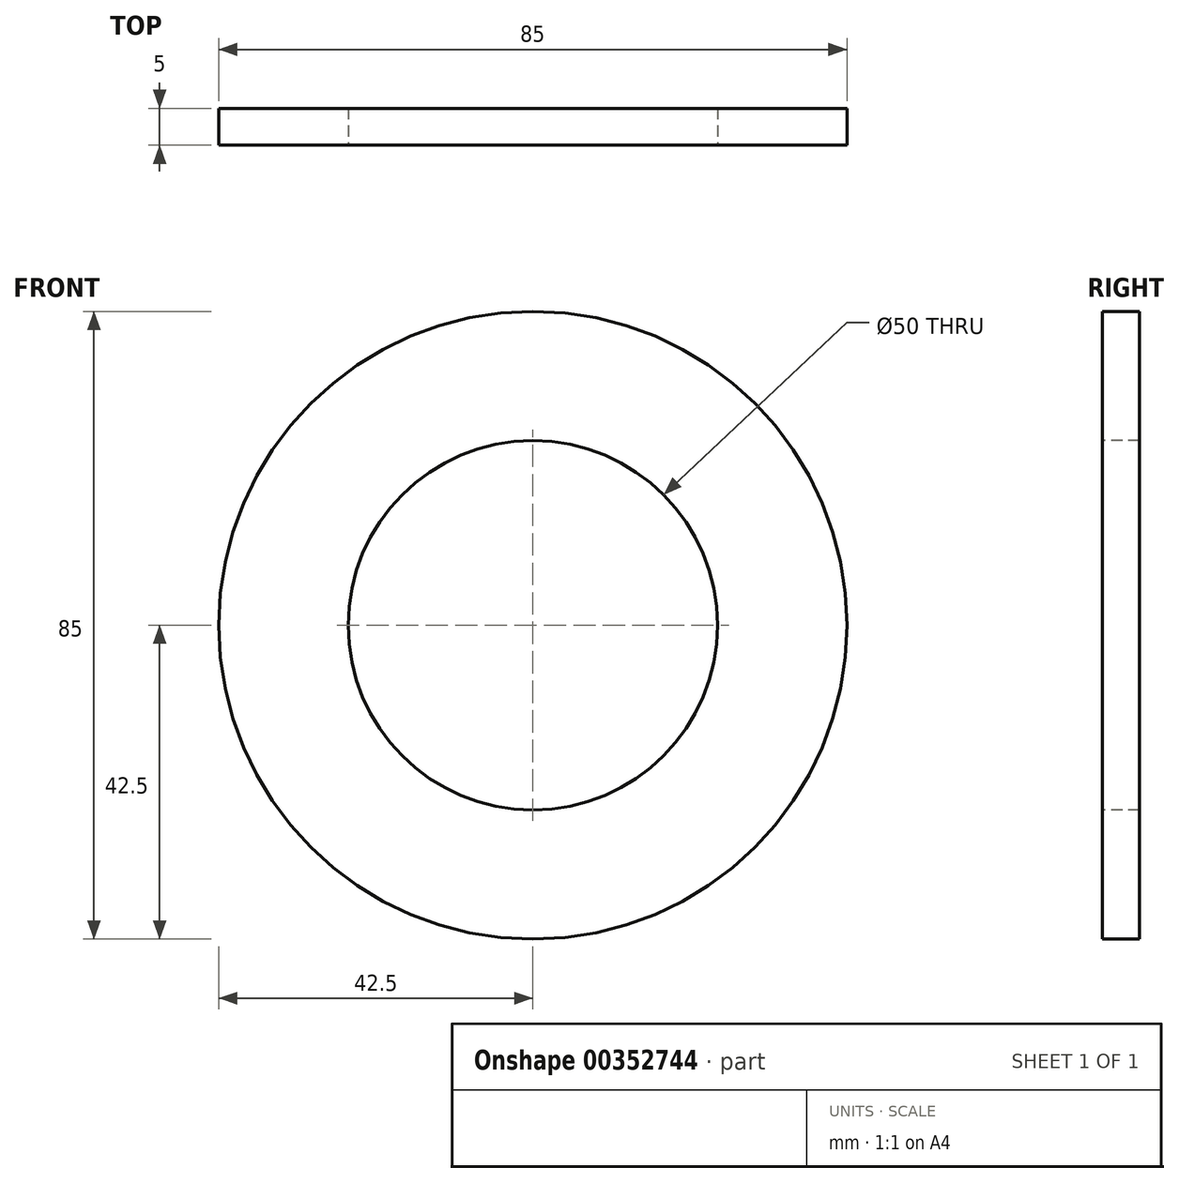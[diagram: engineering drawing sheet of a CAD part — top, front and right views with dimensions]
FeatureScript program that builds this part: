
annotation { "Feature Type Name" : "Feature", "Feature Type Description" : "" }
export const myFeature = defineFeature(function(context is Context, id is Id, definition is map)
    precondition{}
    {
        {
            var Q0;
            Q0=qCreatedBy(makeId("Front.planeOp"),FACE);
            var sketch = newSketch(context, id + "F0", { "sketchPlane" : qUnion([Q0])});
            skCircle(sketch, "E0", {"center": v(0, 0) * mm, "radius": 25 * mm});
            skCircle(sketch, "E1", {"center": v(0, 0) * mm, "radius": 42.5 * mm});
            skSolve(sketch);
        }
        {
            var Q0;
            Q0=makeQuery(id+"F0.imprint","IMPRINT",FACE,{"disambiguationData":[TD([[makeQuery(id+"F0.imprint","IMPRINT",EDGE,{"derivedFrom":sQuery(id+"F0.wireOp",EDGE,"E0")}),-1.0]])]});
            extrude(context, id + "F1", {"entities" : qUnion([Q0]), "oppositeDirection" : true, "depth" : 5 * mm});
        }
    });
